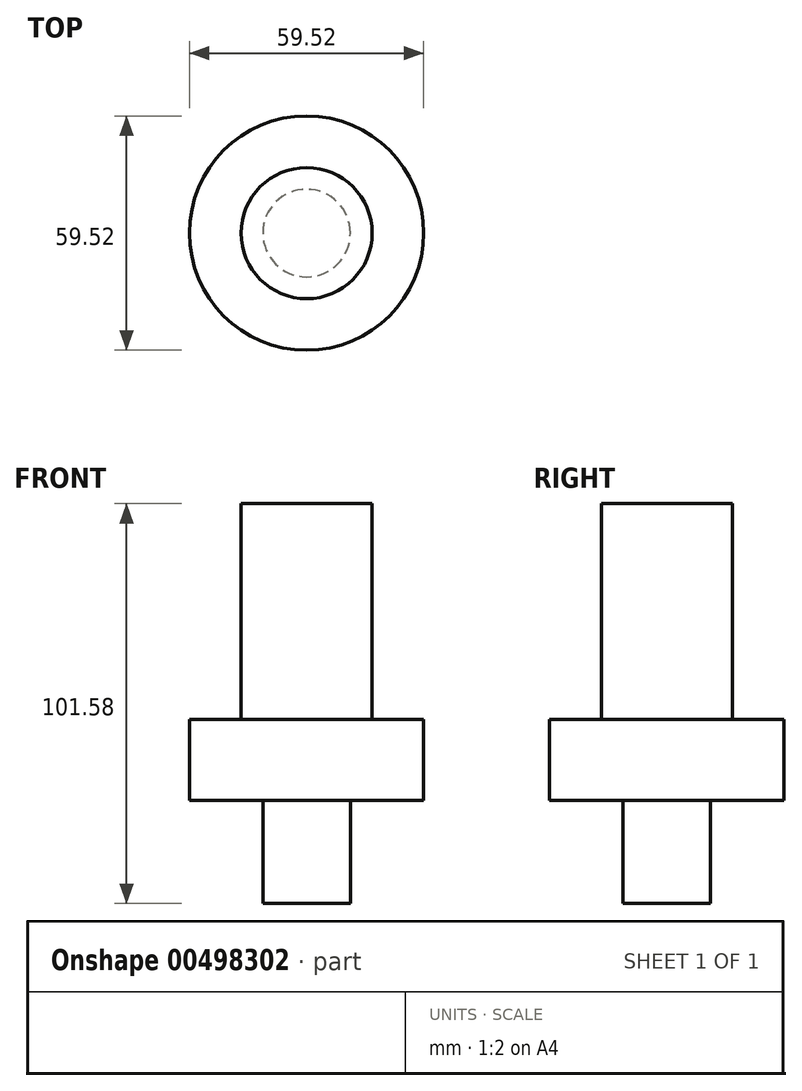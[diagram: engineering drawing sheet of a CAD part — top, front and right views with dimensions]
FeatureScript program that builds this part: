
annotation { "Feature Type Name" : "Feature", "Feature Type Description" : "" }
export const myFeature = defineFeature(function(context is Context, id is Id, definition is map)
    precondition{}
    {
        {
            var Q0;
            Q0=qCreatedBy(makeId("Top.planeOp"),FACE);
            var sketch = newSketch(context, id + "F0", { "sketchPlane" : qUnion([Q0])});
            skCircle(sketch, "E0", {"center": v(0, 0) * mm, "radius": 16.66 * mm});
            skSolve(sketch);
        }
        {
            var Q0;
            Q0 = qSketchRegion(id + "F0", true);
            extrude(context, id + "F1", {"entities" : qUnion([Q0]), "depth" : 54.77 * mm});
        }
        {
            var Q0;
            Q0=makeQuery(id+"F1.opExtrude","CAP_FACE",FACE,{"disambiguationData":[OSD([sQuery(id+"F0.wireOp",EDGE,"E0")])],"isStart":true});
            var sketch = newSketch(context, id + "F2", { "sketchPlane" : qUnion([Q0])});
            skCircle(sketch, "E1", {"center": v(0, 0) * mm, "radius": 29.76 * mm});
            skSolve(sketch);
        }
        {
            var Q0;
            Q0 = qSketchRegion(id + "F2", true);
            extrude(context, id + "F3", {"entities" : qUnion([Q0]), "operationType" : NewBodyOperationType.ADD, "depth" : 20.62 * mm});
        }
        {
            var Q0;
            Q0=makeQuery(id+"F3.opExtrude","CAP_FACE",FACE,{"disambiguationData":[OSD([sQuery(id+"F2.wireOp",EDGE,"E1")])],"isStart":false});
            var sketch = newSketch(context, id + "F4", { "sketchPlane" : qUnion([Q0])});
            skCircle(sketch, "E2", {"center": v(0, 0) * mm, "radius": 11.11 * mm});
            skSolve(sketch);
        }
        {
            var Q0;
            Q0=makeQuery(id+"F4.imprint","IMPRINT",FACE,{"disambiguationData":[TD([[makeQuery(id+"F4.imprint","IMPRINT",EDGE,{"derivedFrom":sQuery(id+"F4.wireOp",EDGE,"E2")}),1.0]])]});
            extrude(context, id + "F5", {"entities" : qUnion([Q0]), "operationType" : NewBodyOperationType.ADD, "depth" : 26.2 * mm});
        }
    });
